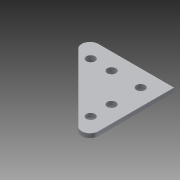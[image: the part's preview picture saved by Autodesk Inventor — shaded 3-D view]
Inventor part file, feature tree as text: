
AUTODESK INVENTOR PART (.ipt)
format: ipt  version: 2013 (Build 170138000, 138)  size: 103,936 bytes
history: native  units: in
note: dims shown in document units (in); Inventor stores cm internally (conversion verified against a paired STEP export)
features: extrude x1, fillet x1, sketch x1
ambient origin geometry x8: Origin, YZ Plane, XZ Plane, XY Plane, X Axis, Y Axis, Z Axis, Center Point
bodies: Solid1 (feature_tree)
feature tree (3):
  extrude  "Extrusion1"  Depth=2.875in
  fillet  "Fillet1"  Radius=0.5in
  sketch  "Sketch1"  dims[d0=2.875in d1=2.875in d2=0.5in d3=0.5in d4=0.26in d5=0.26in d6=0.26in d7=0.26in d8=0.625in d9=0.625in d10=0.26in d11=0.125in d12=0.0in d13=0.25in d14=1.375in d15=1.375in]
